# Revit family: Plymold-Essentials-Round_Drop_Top-Waste_Receptacle
name_source: partatom
category: Furniture
units: mm (PartAtom-declared; Revit-internal decimal feet)

## family parameters
Always vertical = Yes
Cut with Voids When Loaded = No
OmniClass Number = 23.40.20.00
OmniClass Title = General Furniture and Specialties
Render Appearance Source = Family Geometry
Room Calculation Point = No
Shared = No
Work Plane-Based = No

## types (2) — shared parameters
Assembly Code = E2020200
BACK MATERIAL = PLY - Solid Oak Vertical
Brand = Receptacle
DIVIDER MATERIAL = PLY - Solid Oak Vertical
DOOR MATERIAL = PLY - Solid Oak Vertical
Default Elevation = 0"
Depth = 26"
EDGE HORIZONTAL MATERIAL = PLY - Solid Oak Horizontal
EDGE VERTICAL MATERIAL = PLY - Solid Oak Vertical
GLIDES MATERIAL = PLY - Plastic Black
HARDWARE MATERIAL = PLY - Onyx Black Powdercoat
Height = 48"
Keynote = 12500
Manufacturer = Plymold
PLASTIC MATERIAL = PLY - Plastic Black
PULL MATERIAL = PLY - Metal_Galvanized
Product Documentation Link = https://plymold.com
Revit Model Built By = https://www.servex-us.com
SIDE MATERIAL = PLY - Solid Oak Vertical
Sustainability = https://plymold.com
TOP EDGE MATERIAL = PLY - Plastic Black
TOP MATERIAL = PLY - Solid Oak Horizontal
Type Comments = Casegoods
URL = https://plymold.com
zero-valued in all types: Cost

## per-type parameters (varying)
| type | Description | Width |
| 80111DE | Round Drop Top Waste Receptacle with Tray Shelf - 26"W x 26"D x 48"H | 26" |
| 80112DE | Double Round Drop Top Waste Receptacle with Tray Shelf - 48"W x 26"D x 48"H | 48" |

note: column(s) folded — value = type name in every type: Model

## geometry (parser evidence)
native form markers: Sweep x10
no freeform markers — native parametric forms only
